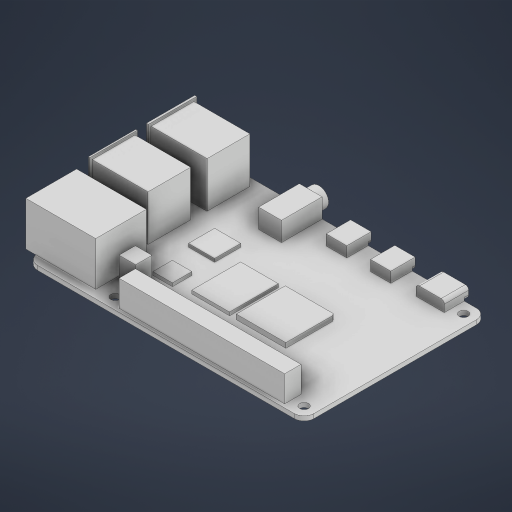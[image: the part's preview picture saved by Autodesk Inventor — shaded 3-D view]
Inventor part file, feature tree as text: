
AUTODESK INVENTOR PART (.ipt)
format: ipt  version: 2024 (Build 280153000, 153)  size: 572,416 bytes
history: native  units: in
note: dims shown in document units (in); Inventor stores cm internally (conversion verified against a paired STEP export)
features: extrude x11, sketch x6, projected_geometry x5, fillet x1, other x1
ambient origin geometry x8: Origin, YZ Plane, XZ Plane, XY Plane, X Axis, Y Axis, Z Axis, Center Point
bodies: Solid1 (feature_tree)
feature tree (24):
  sketch  "Sketch2"  dims[d21=3.7in d72=0.1063in]
  extrude  "Extrusion1"  Depth=2.2047in
  sketch  "Sketch3"  dims[d73=0.1378in d74=0.1378in]
  extrude  "Extrusion2"  Depth=0.1063in
  extrude  "Extrusion3"  Depth=0.1378in
  extrude  "Extrusion4"  Depth=0.2362in
  extrude  "Extrusion5"  Depth=0.1378in
  extrude  "Extrusion6"  Depth=0.0394in
  extrude  "Extrusion7"  Depth=0.2362in
  extrude  "Extrusion8"  Depth=0.0394in
  extrude  "Extrusion9"  Depth=0.0394in
  extrude  "Extrusion10"  Depth=0.2362in
  extrude  "Extrusion11"  Depth=0.125in
  fillet  "Fillet1"  Radius=0.1181in
  sketch  "Sketch1"  dims[d0=3.3465in d1=2.2047in]
  other  "Image1"
  projected_geometry  "Projected Loop1"
  sketch  "Sketch4"  dims[d75=0.2362in d76=0.2362in]
  projected_geometry  "Projected Loop2"
  sketch  "Sketch5"  dims[d77=0.1063in d78=0.1378in]
  sketch  "Sketch6"  dims[d79=0.1378in d80=0.1063in d81=0.2362in d82=2.2835in d88=0.1063in d89=0.2362in d90=0.125in d91=0.1181in d92=0.0531in d93=0.0in d94=0.5512in d95=0.0in d96=0.5315in d97=0.0in d98=0.0591in d99=0.0in d100=0.0394in d101=0.0in d102=0.315in d103=0.0in d104=0.1268in d105=0.0in d106=0.2331in d107=0.0in d108=0.0984in d109=0.0in d110=0.586in d111=0.035in d112=0.0in d113=0.0in d114=0.586in d115=0.0in d116=0.0394in]
  projected_geometry  "Projected Loop3"
  projected_geometry  "Projected Loop4"
  projected_geometry  "Projected Loop5"
